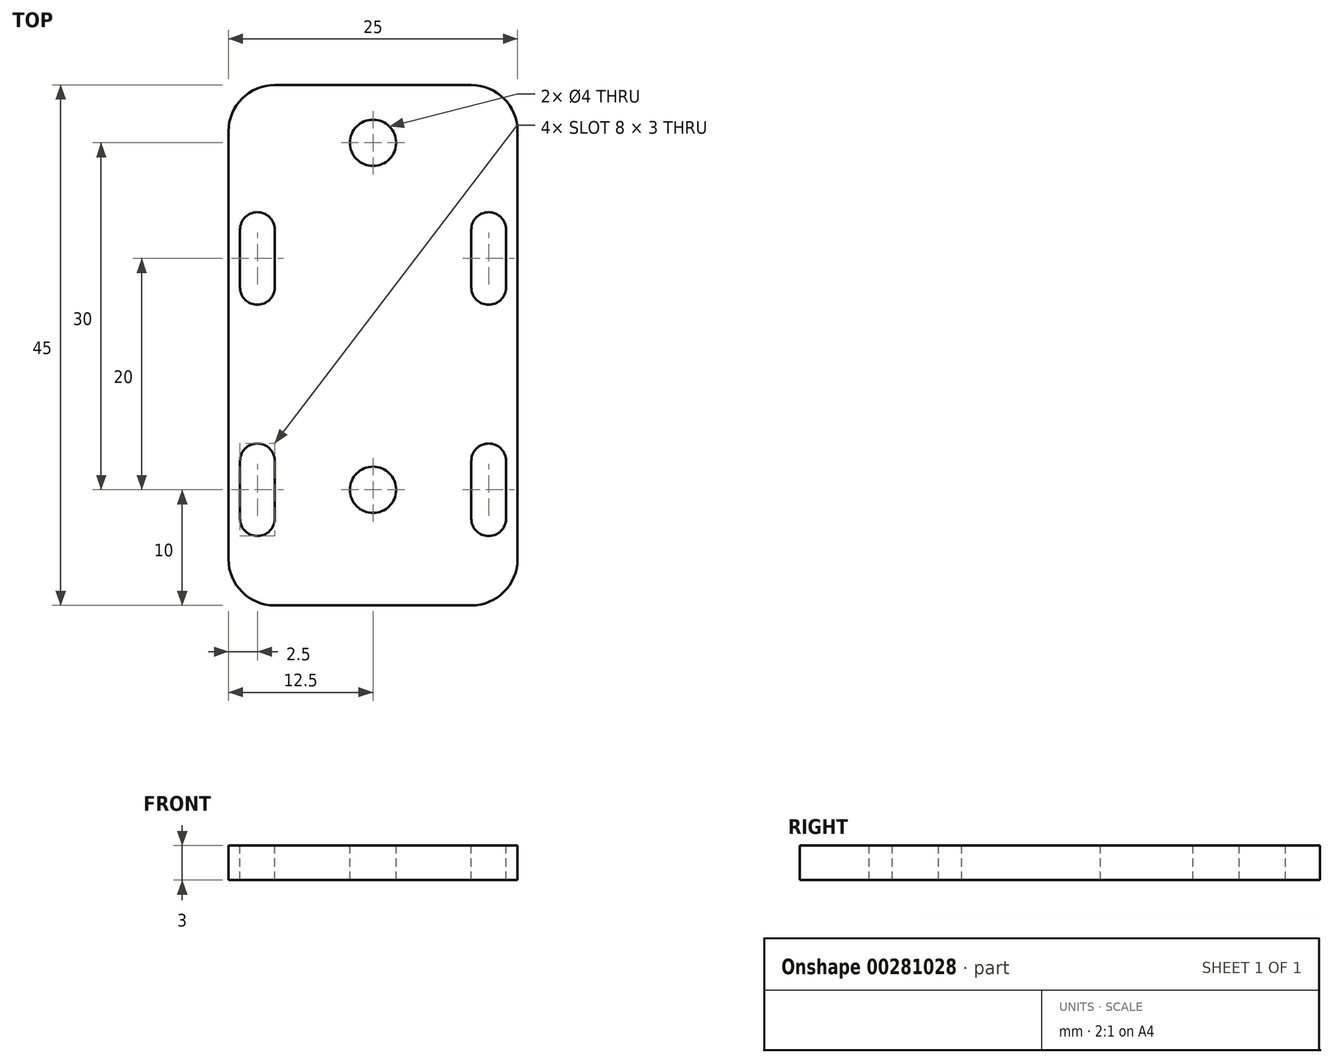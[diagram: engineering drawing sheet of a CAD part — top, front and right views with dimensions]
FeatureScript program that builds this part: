
annotation { "Feature Type Name" : "Feature", "Feature Type Description" : "" }
export const myFeature = defineFeature(function(context is Context, id is Id, definition is map)
    precondition{}
    {
        {
            var Q0;
            Q0=qCreatedBy(makeId("Top.planeOp"),FACE);
            var sketch = newSketch(context, id + "F0", { "sketchPlane" : qUnion([Q0])});
            skLineSegment(sketch, "E0.bottom", {"start": v(8.5, -22.5) * mm, "end": v(-8.5, -22.5) * mm});
            skLineSegment(sketch, "E0.top", {"start": v(8.5, 22.5) * mm, "end": v(-8.5, 22.5) * mm});
            skLineSegment(sketch, "E0.left", {"start": v(12.5, -18.5) * mm, "end": v(12.5, 18.5) * mm});
            skLineSegment(sketch, "E0.right", {"start": v(-12.5, -18.5) * mm, "end": v(-12.5, 18.5) * mm});
            skPoint(sketch, "E0.middle", {"position": v(0, 0) * mm});
            skPoint(sketch, "E1.visualSharp", {"position": v(-12.5, 22.5) * mm});
            skArc(sketch, "E1.filletArc", {"start": v(-8.5, 22.5) * mm, "mid": v(-11.33, 21.33) * mm, "end": v(-12.5, 18.5) * mm});
            skPoint(sketch, "E2.visualSharp", {"position": v(12.5, 22.5) * mm});
            skArc(sketch, "E2.filletArc", {"start": v(12.5, 18.5) * mm, "mid": v(11.33, 21.33) * mm, "end": v(8.5, 22.5) * mm});
            skPoint(sketch, "E3.visualSharp", {"position": v(12.5, -22.5) * mm});
            skArc(sketch, "E3.filletArc", {"start": v(8.5, -22.5) * mm, "mid": v(11.33, -21.33) * mm, "end": v(12.5, -18.5) * mm});
            skPoint(sketch, "E4.visualSharp", {"position": v(-12.5, -22.5) * mm});
            skArc(sketch, "E4.filletArc", {"start": v(-12.5, -18.5) * mm, "mid": v(-11.33, -21.33) * mm, "end": v(-8.5, -22.5) * mm});
            skSolve(sketch);
        }
        {
            var Q0;
            Q0=makeQuery(id+"F0.imprint","IMPRINT",FACE,{"disambiguationData":[TD([[makeQuery(id+"F0.imprint","IMPRINT",EDGE,{"derivedFrom":sQuery(id+"F0.wireOp",EDGE,"E0.bottom")}),-1.0]])]});
            extrude(context, id + "F1", {"entities" : qUnion([Q0]), "depth" : 3 * mm});
        }
        {
            var Q0;
            Q0=makeQuery(id+"F1.opExtrude","CAP_FACE",FACE,{"disambiguationData":[OSD([sQuery(id+"F0.wireOp",EDGE,"E0.bottom"),sQuery(id+"F0.wireOp",EDGE,"E0.top"),sQuery(id+"F0.wireOp",EDGE,"E0.left"),sQuery(id+"F0.wireOp",EDGE,"E0.right"),sQuery(id+"F0.wireOp",EDGE,"E1.filletArc"),sQuery(id+"F0.wireOp",EDGE,"E2.filletArc"),sQuery(id+"F0.wireOp",EDGE,"E3.filletArc"),sQuery(id+"F0.wireOp",EDGE,"E4.filletArc")])],"isStart":false});
            var sketch = newSketch(context, id + "F2", { "sketchPlane" : qUnion([Q0])});
            skLineSegment(sketch, "E5", {"start": v(-10, 10) * mm, "end": v(-10, 5) * mm, "construction": true});
            skLineSegment(sketch, "E6", {"start": v(-10, -10) * mm, "end": v(-10, -15) * mm, "construction": true});
            skLineSegment(sketch, "E7", {"start": v(10, -10) * mm, "end": v(10, -15) * mm, "construction": true});
            skLineSegment(sketch, "E8", {"start": v(10, 10) * mm, "end": v(10, 5) * mm, "construction": true});
            skLineSegment(sketch, "E9", {"start": v(-10, 7.5) * mm, "end": v(10, 7.5) * mm, "construction": true});
            skLineSegment(sketch, "E10", {"start": v(10, -12.5) * mm, "end": v(-10, -12.5) * mm, "construction": true});
            skPoint(sketch, "E10.endSnap0", {"position": v(-10, -12.5) * mm});
            skLineSegment(sketch, "E11", {"start": v(0, 7.5) * mm, "end": v(0, -12.5) * mm, "construction": true});
            skCircle(sketch, "E12", {"center": v(0, -12.5) * mm, "radius": 2 * mm});
            skCircle(sketch, "E13", {"center": v(0, 17.5) * mm, "radius": 2 * mm});
            skArc(sketch, "E14.0.startCap", {"start": v(-11.5, 10) * mm, "mid": v(-10, 11.5) * mm, "end": v(-8.5, 10) * mm});
            skArc(sketch, "E14.0.endCap", {"start": v(-8.5, 5) * mm, "mid": v(-10, 3.5) * mm, "end": v(-11.5, 5) * mm});
            skLineSegment(sketch, "E14.0.left", {"start": v(-8.5, 10) * mm, "end": v(-8.5, 5) * mm});
            skLineSegment(sketch, "E14.0.right", {"start": v(-11.5, 10) * mm, "end": v(-11.5, 5) * mm});
            skArc(sketch, "E14.1.startCap", {"start": v(8.5, 10) * mm, "mid": v(10, 11.5) * mm, "end": v(11.5, 10) * mm});
            skArc(sketch, "E14.1.endCap", {"start": v(11.5, 5) * mm, "mid": v(10, 3.5) * mm, "end": v(8.5, 5) * mm});
            skLineSegment(sketch, "E14.1.left", {"start": v(11.5, 10) * mm, "end": v(11.5, 5) * mm});
            skLineSegment(sketch, "E14.1.right", {"start": v(8.5, 10) * mm, "end": v(8.5, 5) * mm});
            skArc(sketch, "E14.2.startCap", {"start": v(8.5, -10) * mm, "mid": v(10, -8.5) * mm, "end": v(11.5, -10) * mm});
            skArc(sketch, "E14.2.endCap", {"start": v(11.5, -15) * mm, "mid": v(10, -16.5) * mm, "end": v(8.5, -15) * mm});
            skLineSegment(sketch, "E14.2.left", {"start": v(11.5, -10) * mm, "end": v(11.5, -15) * mm});
            skLineSegment(sketch, "E14.2.right", {"start": v(8.5, -10) * mm, "end": v(8.5, -15) * mm});
            skArc(sketch, "E14.3.startCap", {"start": v(-11.5, -10) * mm, "mid": v(-10, -8.5) * mm, "end": v(-8.5, -10) * mm});
            skArc(sketch, "E14.3.endCap", {"start": v(-8.5, -15) * mm, "mid": v(-10, -16.5) * mm, "end": v(-11.5, -15) * mm});
            skLineSegment(sketch, "E14.3.left", {"start": v(-8.5, -10) * mm, "end": v(-8.5, -15) * mm});
            skLineSegment(sketch, "E14.3.right", {"start": v(-11.5, -10) * mm, "end": v(-11.5, -15) * mm});
            skSolve(sketch);
        }
        {
            var Q0;
            Q0 = qSketchRegion(id + "F2", true);
            extrude(context, id + "F3", {"entities" : qUnion([Q0]), "operationType" : NewBodyOperationType.REMOVE, "endBound" : BoundingType.UP_TO_NEXT, "oppositeDirection" : true, "depth" : 25 * mm});
        }
    });
